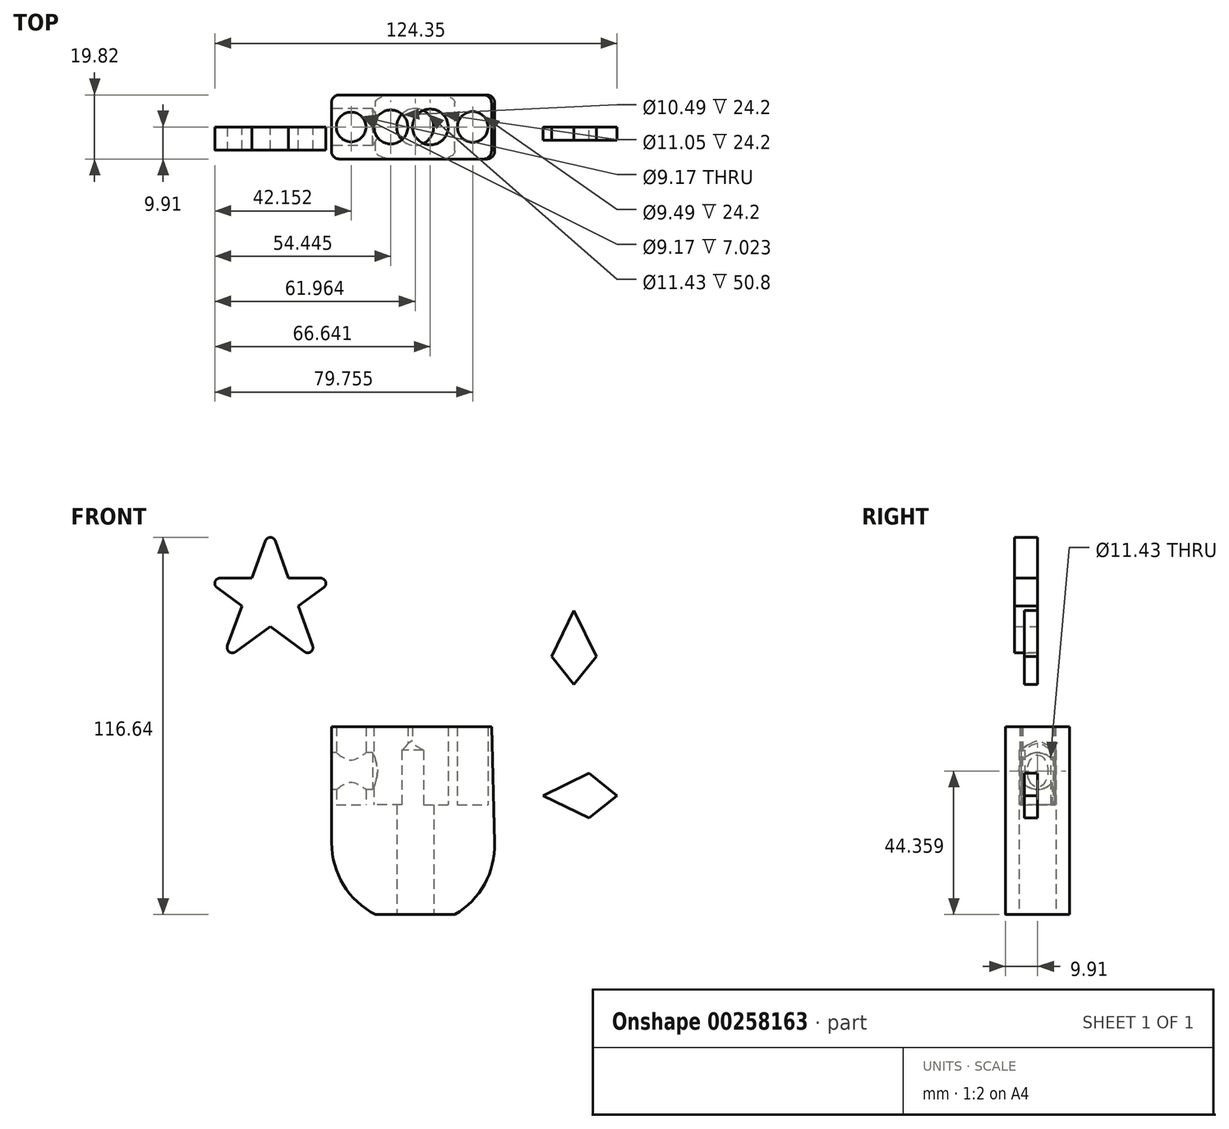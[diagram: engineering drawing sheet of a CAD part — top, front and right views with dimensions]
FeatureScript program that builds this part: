
annotation { "Feature Type Name" : "Feature", "Feature Type Description" : "" }
export const myFeature = defineFeature(function(context is Context, id is Id, definition is map)
    precondition{}
    {
        {
            var Q0;
            Q0=qCreatedBy(makeId("Front.planeOp"),FACE);
            var sketch = newSketch(context, id + "F0", { "sketchPlane" : qUnion([Q0])});
            skLineSegment(sketch, "E0", {"start": v(-38.07, 24.2) * mm, "end": v(11.46, 24.2) * mm});
            skArc(sketch, "E1", {"start": v(-36.75, -44.32) * mm, "mid": v(-33.39, -56.95) * mm, "end": v(-24.56, -66.6) * mm});
            skArc(sketch, "E2", {"start": v(11.46, -44.32) * mm, "mid": v(8.43, -56.84) * mm, "end": v(0, -66.6) * mm});
            skLineSegment(sketch, "E3", {"start": v(-38.07, 24.2) * mm, "end": v(-38, -11.72) * mm});
            skLineSegment(sketch, "E4", {"start": v(-24.56, -66.6) * mm, "end": v(0, -66.6) * mm});
            skLineSegment(sketch, "E5", {"start": v(11.46, 24.2) * mm, "end": v(12.42, -11.72) * mm});
            skLineSegment(sketch, "E6", {"start": v(-24.43, -33.93) * mm, "end": v(0.13, -33.93) * mm});
            skArc(sketch, "E7", {"start": v(-38, -11.72) * mm, "mid": v(-34.33, -24.73) * mm, "end": v(-24.43, -33.93) * mm});
            skArc(sketch, "E8", {"start": v(12.42, -11.72) * mm, "mid": v(9.3, -24.5) * mm, "end": v(0.13, -33.93) * mm});
            skPoint(sketch, "E9", {"position": v(-23.45, 24.2) * mm});
            skPoint(sketch, "E10", {"position": v(-5.89, 24.2) * mm});
            skSolve(sketch);
        }
        {
            var Q0;
            Q0=makeQuery(id+"F0.imprint","IMPRINT",FACE,{"disambiguationData":[TD([[makeQuery(id+"F0.imprint","IMPRINT",EDGE,{"derivedFrom":sQuery(id+"F0.wireOp",EDGE,"E0")}),-1.0]])]});
            extrude(context, id + "F1", {"entities" : qUnion([Q0]), "endBound" : BoundingType.SYMMETRIC, "depth" : 19.8 * mm});
        }
        {
            var Q0;
            Q0=qCreatedBy(makeId("Top.planeOp"),FACE);
            var sketch = newSketch(context, id + "F2", { "sketchPlane" : qUnion([Q0])});
            skCircle(sketch, "E11", {"center": v(5.64, 0) * mm, "radius": 4.82 * mm});
            skCircle(sketch, "E12", {"center": v(-19.68, 0) * mm, "radius": 5.24 * mm});
            skCircle(sketch, "E13", {"center": v(-7.48, 0) * mm, "radius": 5.52 * mm});
            skCircle(sketch, "E14", {"center": v(-31.97, 0) * mm, "radius": 4.58 * mm});
            skSolve(sketch);
        }
        {
            var Q0;
            Q0=sQuery(id+"F2.wireOp",VERTEX,"E12.center");
            var Q1;
            Q1=makeQuery(id+"F1.opExtrude","SWEPT_BODY",BODY,{"disambiguationData":[OSD([sQuery(id+"F0.wireOp",EDGE,"E0"),sQuery(id+"F0.wireOp",EDGE,"HOkLMQzX-Mq7s-O9GJ-osXQ-mvmMlddkdkxN"),sQuery(id+"F0.wireOp",EDGE,"E1"),sQuery(id+"F0.wireOp",EDGE,"E2"),sQuery(id+"F0.wireOp",EDGE,"D0J2uPAa-b80y-GPz8-SfUj-J0MItKTl9xqN"),sQuery(id+"F0.wireOp",EDGE,"3hHQtNDz-Hd3L-nIIW-E9C7-DY1hk1zCaixw"),sQuery(id+"F0.wireOp",EDGE,"E3")])]});
            hole(context, id + "F3", {"style" : HoleStyle.SIMPLE, "endStyle" : HoleEndStyle.BLIND, "oppositeDirection" : true, "holeDiameter" : 10.5 * mm, "holeDepth" : 25.4 * mm, "tappedDepth" : 12.7 * mm, "tapClearance" : 3, "locations" : qUnion([Q0]), "scope" : qUnion([Q1])});
        }
        {
            var Q0;
            Q0=sQuery(id+"F2.wireOp",VERTEX,"E13.center");
            var Q1;
            Q1=makeQuery(id+"F1.opExtrude","SWEPT_BODY",BODY,{"disambiguationData":[OSD([sQuery(id+"F0.wireOp",EDGE,"E0"),sQuery(id+"F0.wireOp",EDGE,"HOkLMQzX-Mq7s-O9GJ-osXQ-mvmMlddkdkxN"),sQuery(id+"F0.wireOp",EDGE,"E1"),sQuery(id+"F0.wireOp",EDGE,"E2"),sQuery(id+"F0.wireOp",EDGE,"D0J2uPAa-b80y-GPz8-SfUj-J0MItKTl9xqN"),sQuery(id+"F0.wireOp",EDGE,"3hHQtNDz-Hd3L-nIIW-E9C7-DY1hk1zCaixw"),sQuery(id+"F0.wireOp",EDGE,"E3")])]});
            hole(context, id + "F4", {"style" : HoleStyle.SIMPLE, "endStyle" : HoleEndStyle.BLIND, "oppositeDirection" : true, "holeDiameter" : 11.05 * mm, "holeDepth" : 25.4 * mm, "tappedDepth" : 12.7 * mm, "tapClearance" : 3, "locations" : qUnion([Q0]), "scope" : qUnion([Q1])});
        }
        {
            var Q0;
            Q0=sQuery(id+"F2.wireOp",VERTEX,"E11.center");
            var Q1;
            Q1=makeQuery(id+"F1.opExtrude","SWEPT_BODY",BODY,{"disambiguationData":[OSD([sQuery(id+"F0.wireOp",EDGE,"E0"),sQuery(id+"F0.wireOp",EDGE,"HOkLMQzX-Mq7s-O9GJ-osXQ-mvmMlddkdkxN"),sQuery(id+"F0.wireOp",EDGE,"E1"),sQuery(id+"F0.wireOp",EDGE,"E2"),sQuery(id+"F0.wireOp",EDGE,"D0J2uPAa-b80y-GPz8-SfUj-J0MItKTl9xqN"),sQuery(id+"F0.wireOp",EDGE,"3hHQtNDz-Hd3L-nIIW-E9C7-DY1hk1zCaixw"),sQuery(id+"F0.wireOp",EDGE,"E3")])]});
            hole(context, id + "F5", {"style" : HoleStyle.SIMPLE, "endStyle" : HoleEndStyle.BLIND, "oppositeDirection" : true, "holeDiameter" : 9.5 * mm, "holeDepth" : 25.4 * mm, "tappedDepth" : 12.7 * mm, "tapClearance" : 3, "locations" : qUnion([Q0]), "scope" : qUnion([Q1])});
        }
        {
            var Q0;
            Q0=sQuery(id+"F2.wireOp",VERTEX,"E14.center");
            var Q1;
            Q1=makeQuery(id+"F1.opExtrude","SWEPT_BODY",BODY,{"disambiguationData":[OSD([sQuery(id+"F0.wireOp",EDGE,"E0"),sQuery(id+"F0.wireOp",EDGE,"HOkLMQzX-Mq7s-O9GJ-osXQ-mvmMlddkdkxN"),sQuery(id+"F0.wireOp",EDGE,"E1"),sQuery(id+"F0.wireOp",EDGE,"E2"),sQuery(id+"F0.wireOp",EDGE,"D0J2uPAa-b80y-GPz8-SfUj-J0MItKTl9xqN"),sQuery(id+"F0.wireOp",EDGE,"3hHQtNDz-Hd3L-nIIW-E9C7-DY1hk1zCaixw"),sQuery(id+"F0.wireOp",EDGE,"E3")])]});
            hole(context, id + "F6", {"style" : HoleStyle.SIMPLE, "endStyle" : HoleEndStyle.BLIND, "oppositeDirection" : true, "holeDiameter" : 9.17 * mm, "holeDepth" : 25.4 * mm, "tappedDepth" : 12.7 * mm, "tapClearance" : 3, "locations" : qUnion([Q0]), "scope" : qUnion([Q1])});
        }
        {
            var Q0;
            Q0=makeQuery(id+"F1.opExtrude","SWEPT_FACE",FACE,{"disambiguationData":[OSD([sQuery(id+"F0.wireOp",EDGE,"E3")])]});
            var sketch = newSketch(context, id + "F7", { "sketchPlane" : qUnion([Q0])});
            skPoint(sketch, "E15.middle", {"position": v(16.14, 9.4) * mm});
            skLineSegment(sketch, "E16.bottom", {"start": v(-5.62, 0) * mm, "end": v(5.62, 0) * mm});
            skLineSegment(sketch, "E16.top", {"start": v(-5.62, 20.98) * mm, "end": v(5.62, 20.98) * mm});
            skLineSegment(sketch, "E16.left", {"start": v(-5.62, 0) * mm, "end": v(-5.62, 20.98) * mm});
            skLineSegment(sketch, "E16.right", {"start": v(5.62, 0) * mm, "end": v(5.62, 20.98) * mm});
            skPoint(sketch, "E16.middle", {"position": v(0, 10.5) * mm});
            skSolve(sketch);
        }
        {
            var Q0;
            Q0=sQuery(id+"F7.wireOp",VERTEX,"E16.middle");
            var Q1;
            Q1=makeQuery(id+"F1.opExtrude","SWEPT_BODY",BODY,{"disambiguationData":[OSD([sQuery(id+"F0.wireOp",EDGE,"E0"),sQuery(id+"F0.wireOp",EDGE,"HOkLMQzX-Mq7s-O9GJ-osXQ-mvmMlddkdkxN"),sQuery(id+"F0.wireOp",EDGE,"E1"),sQuery(id+"F0.wireOp",EDGE,"E2"),sQuery(id+"F0.wireOp",EDGE,"D0J2uPAa-b80y-GPz8-SfUj-J0MItKTl9xqN"),sQuery(id+"F0.wireOp",EDGE,"3hHQtNDz-Hd3L-nIIW-E9C7-DY1hk1zCaixw"),sQuery(id+"F0.wireOp",EDGE,"E3")])]});
            hole(context, id + "F8", {"style" : HoleStyle.SIMPLE, "endStyle" : HoleEndStyle.BLIND, "holeDiameter" : 11.43 * mm, "holeDepth" : 12.7 * mm, "tappedDepth" : 12.7 * mm, "tapClearance" : 3, "locations" : qUnion([Q0]), "scope" : qUnion([Q1])});
        }
        {
            var Q0;
            Q0=qCreatedBy(makeId("Front.planeOp"),FACE);
            var sketch = newSketch(context, id + "F9", { "sketchPlane" : qUnion([Q0])});
            skLineSegment(sketch, "E17", {"start": v(-56.93, 85.84) * mm, "end": v(-72, 44.24) * mm});
            skLineSegment(sketch, "E18", {"start": v(-77.42, 70.09) * mm, "end": v(-36.44, 70.09) * mm});
            skLineSegment(sketch, "E19", {"start": v(-36.44, 70.09) * mm, "end": v(-72, 44.24) * mm});
            skLineSegment(sketch, "E20", {"start": v(-77.42, 70.09) * mm, "end": v(-42.12, 44.24) * mm});
            skLineSegment(sketch, "E21", {"start": v(-42.12, 44.24) * mm, "end": v(-56.93, 85.84) * mm});
            skPoint(sketch, "E22", {"position": v(-56.93, 70.09) * mm});
            skSolve(sketch);
        }
        {
            var Q0;
            Q0 = qSketchRegion(id + "F9", true);
            extrude(context, id + "F10", {"entities" : qUnion([Q0]), "operationType" : NewBodyOperationType.ADD, "depth" : 7.11 * mm});
        }
        {
            var Q0;
            Q0=makeQuery(id+"F10.opExtrude","SWEPT_EDGE",EDGE,{"disambiguationData":[OSD([sQuery(id+"F9.wireOp",EDGE,"E18"),sQuery(id+"F9.wireOp",EDGE,"E20")])]});
            var Q1;
            Q1=makeQuery(id+"F10.opExtrude","SWEPT_EDGE",EDGE,{"disambiguationData":[OSD([sQuery(id+"F9.wireOp",EDGE,"E17"),sQuery(id+"F9.wireOp",EDGE,"E21")])]});
            var Q2;
            Q2=makeQuery(id+"F10.opExtrude","SWEPT_EDGE",EDGE,{"disambiguationData":[OSD([sQuery(id+"F9.wireOp",EDGE,"E18"),sQuery(id+"F9.wireOp",EDGE,"E19")])]});
            var Q3;
            Q3=makeQuery(id+"F10.opExtrude","SWEPT_EDGE",EDGE,{"disambiguationData":[OSD([sQuery(id+"F9.wireOp",EDGE,"E17"),sQuery(id+"F9.wireOp",EDGE,"E19")])]});
            var Q4;
            Q4=makeQuery(id+"F10.opExtrude","SWEPT_EDGE",EDGE,{"disambiguationData":[OSD([sQuery(id+"F9.wireOp",EDGE,"E20"),sQuery(id+"F9.wireOp",EDGE,"E21")])]});
            fillet(context, id + "F11", {"entities" : qUnion([Q0, Q1, Q2, Q3, Q4]), "radius" : 1.6 * mm, "tangentPropagation" : true, "allowEdgeOverflow" : false});
        }
        {
            var Q0;
            Q0=makeQuery(id+"F1.opExtrude","SWEPT_FACE",FACE,{"disambiguationData":[OSD([sQuery(id+"F0.wireOp",EDGE,"E6")])]});
            var sketch = newSketch(context, id + "F12", { "sketchPlane" : qUnion([Q0])});
            skCircle(sketch, "E23", {"center": v(-12.16, 0) * mm, "radius": 4.35 * mm});
            skSolve(sketch);
        }
        {
            var Q0;
            Q0=sQuery(id+"F12.wireOp",VERTEX,"E23.center");
            var Q1;
            Q1=makeQuery(id+"F1.opExtrude","SWEPT_BODY",BODY,{"disambiguationData":[OSD([sQuery(id+"F0.wireOp",EDGE,"E0"),sQuery(id+"F0.wireOp",EDGE,"E3"),sQuery(id+"F0.wireOp",EDGE,"E5"),sQuery(id+"F0.wireOp",EDGE,"E6"),sQuery(id+"F0.wireOp",EDGE,"E7"),sQuery(id+"F0.wireOp",EDGE,"E8")])]});
            hole(context, id + "F13", {"style" : HoleStyle.SIMPLE, "endStyle" : HoleEndStyle.BLIND, "holeDiameter" : 11.43 * mm, "holeDepth" : 50.8 * mm, "tappedDepth" : 12.7 * mm, "tapClearance" : 3, "locations" : qUnion([Q0]), "scope" : qUnion([Q1])});
        }
        {
            var Q0;
            Q0=makeQuery(id+"F1.opExtrude","CAP_EDGE",EDGE,{"disambiguationData":[OSD([sQuery(id+"F0.wireOp",EDGE,"E3")])],"isStart":false});
            var Q1;
            Q1=makeQuery(id+"F1.opExtrude","CAP_EDGE",EDGE,{"disambiguationData":[OSD([sQuery(id+"F0.wireOp",EDGE,"E8")])],"isStart":true});
            var Q2;
            Q2=makeQuery(id+"F1.opExtrude","CAP_EDGE",EDGE,{"disambiguationData":[OSD([sQuery(id+"F0.wireOp",EDGE,"E7")])],"isStart":false});
            var Q3;
            Q3=makeQuery(id+"F1.opExtrude","CAP_EDGE",EDGE,{"disambiguationData":[OSD([sQuery(id+"F0.wireOp",EDGE,"E3")])],"isStart":true});
            var Q4;
            Q4=makeQuery(id+"F1.opExtrude","CAP_EDGE",EDGE,{"disambiguationData":[OSD([sQuery(id+"F0.wireOp",EDGE,"E7")])],"isStart":true});
            var Q5;
            Q5=makeQuery(id+"F1.opExtrude","CAP_EDGE",EDGE,{"disambiguationData":[OSD([sQuery(id+"F0.wireOp",EDGE,"E5")])],"isStart":true});
            var Q6;
            Q6=makeQuery(id+"F1.opExtrude","CAP_EDGE",EDGE,{"disambiguationData":[OSD([sQuery(id+"F0.wireOp",EDGE,"E5")])],"isStart":false});
            var Q7;
            Q7=makeQuery(id+"F1.opExtrude","CAP_EDGE",EDGE,{"disambiguationData":[OSD([sQuery(id+"F0.wireOp",EDGE,"E8")])],"isStart":false});
            fillet(context, id + "F14", {"entities" : qUnion([Q0, Q1, Q2, Q3, Q4, Q5, Q6, Q7]), "radius" : 2.45 * mm, "tangentPropagation" : true, "allowEdgeOverflow" : false});
        }
        {
            var Q0;
            Q0=qCreatedBy(makeId("Front.planeOp"),FACE);
            var sketch = newSketch(context, id + "F15", { "sketchPlane" : qUnion([Q0])});
            skLineSegment(sketch, "E24", {"start": v(30.02, 45.84) * mm, "end": v(36.95, 60.13) * mm});
            skLineSegment(sketch, "E25", {"start": v(36.95, 60.13) * mm, "end": v(43.89, 45.84) * mm});
            skLineSegment(sketch, "E26", {"start": v(43.89, 45.84) * mm, "end": v(36.95, 37.22) * mm});
            skLineSegment(sketch, "E27", {"start": v(36.95, 37.22) * mm, "end": v(30.02, 45.84) * mm});
            skLineSegment(sketch, "E28", {"start": v(41.61, -4.07) * mm, "end": v(27.32, 2.87) * mm});
            skLineSegment(sketch, "E29", {"start": v(27.32, 2.87) * mm, "end": v(41.61, 9.8) * mm});
            skLineSegment(sketch, "E30", {"start": v(41.61, 9.8) * mm, "end": v(50.23, 2.87) * mm});
            skLineSegment(sketch, "E31", {"start": v(50.23, 2.87) * mm, "end": v(41.61, -4.07) * mm});
            skSolve(sketch);
        }
        {
            var Q0;
            Q0=makeQuery(id+"F15.imprint","IMPRINT",FACE,{"disambiguationData":[TD([[makeQuery(id+"F15.imprint","IMPRINT",EDGE,{"derivedFrom":sQuery(id+"F15.wireOp",EDGE,"E24")}),-1.0]])]});
            var Q1;
            Q1=makeQuery(id+"F15.imprint","IMPRINT",FACE,{"disambiguationData":[TD([[makeQuery(id+"F15.imprint","IMPRINT",EDGE,{"derivedFrom":sQuery(id+"F15.wireOp",EDGE,"E28")}),-1.0]])]});
            extrude(context, id + "F16", {"entities" : qUnion([Q0, Q1]), "depth" : 4.06 * mm});
        }
    });
